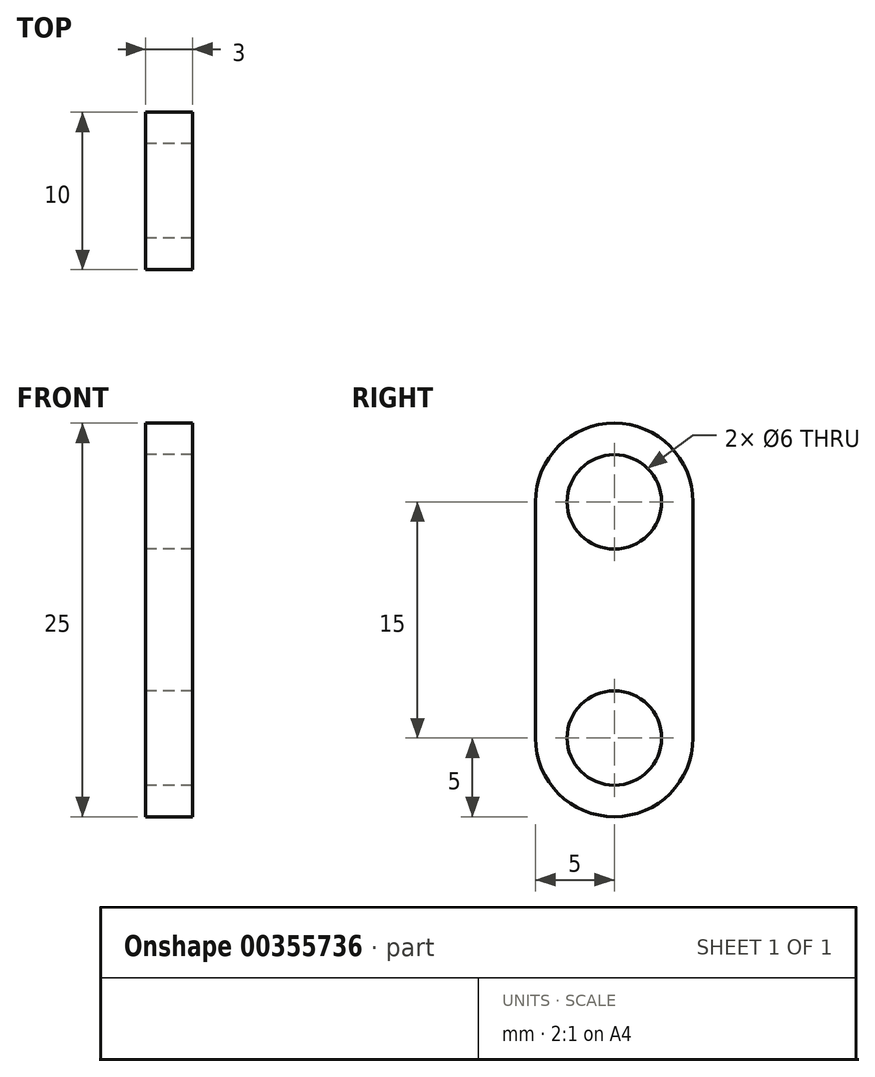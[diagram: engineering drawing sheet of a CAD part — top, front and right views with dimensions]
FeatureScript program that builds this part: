
annotation { "Feature Type Name" : "Feature", "Feature Type Description" : "" }
export const myFeature = defineFeature(function(context is Context, id is Id, definition is map)
    precondition{}
    {
        {
            var Q0;
            Q0=qCreatedBy(makeId("Right.planeOp"),FACE);
            var sketch = newSketch(context, id + "F0", { "sketchPlane" : qUnion([Q0])});
            skLineSegment(sketch, "E0", {"start": v(-5, 0) * mm, "end": v(-5, -15) * mm});
            skLineSegment(sketch, "E1", {"start": v(5, 0) * mm, "end": v(5, -15) * mm});
            skLineSegment(sketch, "E2", {"start": v(-30.93, 0) * mm, "end": v(48.16, 0) * mm, "construction": true});
            skLineSegment(sketch, "E3", {"start": v(-31.4, -15) * mm, "end": v(48.64, -15) * mm, "construction": true});
            skCircle(sketch, "E4", {"center": v(0, 0) * mm, "radius": 3 * mm});
            skCircle(sketch, "E5", {"center": v(0, -15) * mm, "radius": 3 * mm});
            skArc(sketch, "E6", {"start": v(-5, -15) * mm, "mid": v(0, -20) * mm, "end": v(5, -15) * mm});
            skArc(sketch, "E7", {"start": v(5, 0) * mm, "mid": v(0, 5) * mm, "end": v(-5, 0) * mm});
            skSolve(sketch);
        }
        {
            var Q0;
            Q0=makeQuery(id+"F0.imprint","IMPRINT",FACE,{"disambiguationData":[TD([[makeQuery(id+"F0.imprint","IMPRINT",EDGE,{"derivedFrom":sQuery(id+"F0.wireOp",EDGE,"E0")}),1.0]])]});
            extrude(context, id + "F1", {"entities" : qUnion([Q0]), "depth" : 3 * mm});
        }
    });
